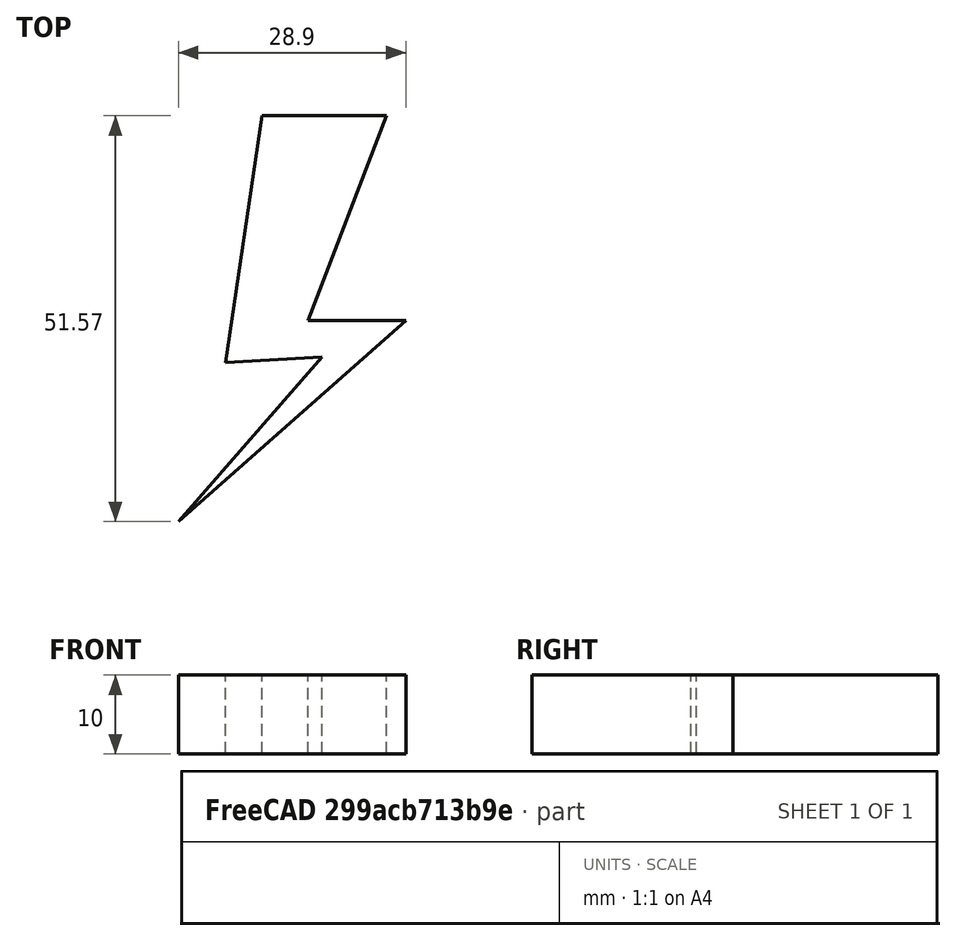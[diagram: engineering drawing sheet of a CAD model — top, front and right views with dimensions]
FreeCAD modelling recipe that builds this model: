
FCSTD DOCUMENT  (FreeCAD 0.21R33694 (Git))
Label: OJT1_T16R01_rayo
License: All rights reserved
LicenseURL: http://en.wikipedia.org/wiki/All_rights_reserved
objects: Sketcher::SketchObject×1, PartDesign::Pad×1, PartDesign::Body×1
note: 4 computed .brp shape members not serialized (recipe doc carries the construction recipe); baked Part::Feature solids carry a one-line shape summary decoded from their .brp

FEATURE [Sketcher::SketchObject] Sketch
  FullyConstrained = false
  MapMode = 5
  Support = -> [XY_Plane]
  sketch-geometry (7):
    g0: LineSegment StartX=0 StartY=19.8884 StartZ=0 EndX=15.834 EndY=19.8884 EndZ=0
    g1: LineSegment StartX=15.834 StartY=19.8884 StartZ=0 EndX=5.83171 EndY=-6.11762 EndZ=0
    g2: LineSegment StartX=5.83171 StartY=-6.11762 StartZ=0 EndX=18.279 EndY=-6.11762 EndZ=0
    g3: LineSegment StartX=18.279 StartY=-6.11762 StartZ=0 EndX=-10.6165 EndY=-31.6791 EndZ=0
    g4: LineSegment StartX=-10.6165 StartY=-31.6791 StartZ=0 EndX=7.6099 EndY=-10.7854 EndZ=0
    g5: LineSegment StartX=7.6099 StartY=-10.7854 StartZ=0 EndX=-4.61514 EndY=-11.4522 EndZ=0
    g6: LineSegment StartX=-4.61514 StartY=-11.4522 StartZ=0 EndX=0 EndY=19.8884 EndZ=0
  constraints (10):
    c: PointOnObject(g0,g-2)
    c: Horizontal(g0)
    c: Coincident(g0,g1)
    c: Coincident(g1,g2)
    c: Horizontal(g2)
    c: Coincident(g2,g3)
    c: Coincident(g3,g4)
    c: Coincident(g4,g5)
    c: Coincident(g5,g6)
    c: Coincident(g6,g0)
FEATURE [PartDesign::Pad] Pad
  Direction = (0,0,1)
  Length = 10
  Length2 = 10
  Profile = -> Sketch
  ReferenceAxis = -> Sketch [N_Axis]
  Type = 0
FEATURE [PartDesign::Body] Body
  Group = -> [Sketch,Pad]
  Origin = -> Origin
  Tip = -> Pad
